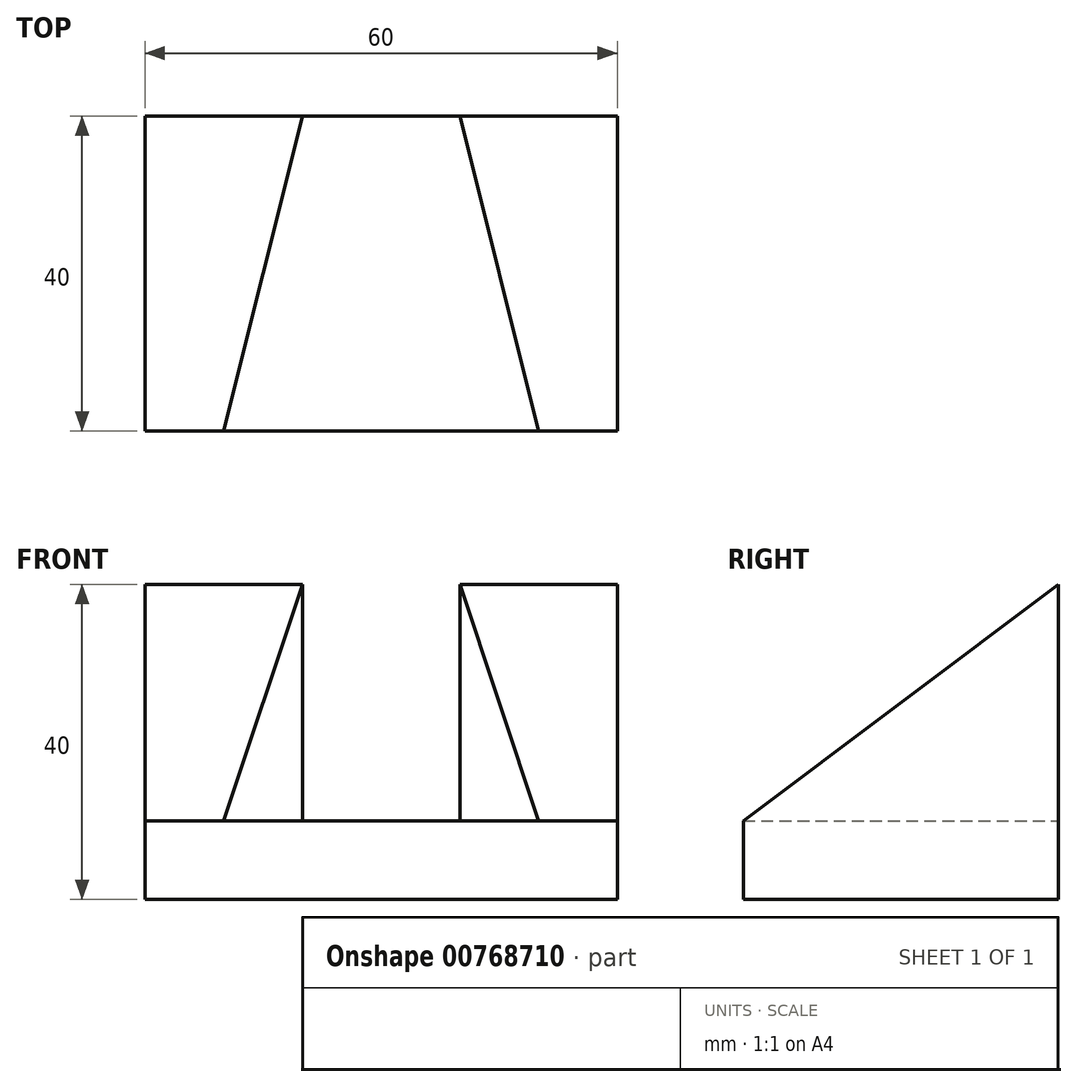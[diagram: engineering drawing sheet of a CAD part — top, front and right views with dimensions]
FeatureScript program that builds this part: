
annotation { "Feature Type Name" : "Feature", "Feature Type Description" : "" }
export const myFeature = defineFeature(function(context is Context, id is Id, definition is map)
    precondition{}
    {
        {
            var Q0;
            Q0=qCreatedBy(makeId("Top.planeOp"),FACE);
            var sketch = newSketch(context, id + "F0", { "sketchPlane" : qUnion([Q0])});
            skLineSegment(sketch, "E0", {"start": v(0, 0) * mm, "end": v(0, 40) * mm});
            skLineSegment(sketch, "E1", {"start": v(0, 40) * mm, "end": v(60, 40) * mm});
            skLineSegment(sketch, "E2", {"start": v(60, 40) * mm, "end": v(60, 0) * mm});
            skLineSegment(sketch, "E3", {"start": v(60, 0) * mm, "end": v(0, 0) * mm});
            skSolve(sketch);
        }
        {
            var Q0;
            Q0=makeQuery(id+"F0.imprint","IMPRINT",FACE,{"disambiguationData":[TD([[makeQuery(id+"F0.imprint","IMPRINT",EDGE,{"derivedFrom":sQuery(id+"F0.wireOp",EDGE,"E0")}),-1.0]])]});
            extrude(context, id + "F1", {"entities" : qUnion([Q0]), "depth" : 40 * mm, "offsetDistance" : 25 * mm});
        }
        {
            var Q0;
            Q0=makeQuery(id+"F1.opExtrude","CAP_FACE",FACE,{"disambiguationData":[OSD([sQuery(id+"F0.wireOp",EDGE,"E0"),sQuery(id+"F0.wireOp",EDGE,"E1"),sQuery(id+"F0.wireOp",EDGE,"E2"),sQuery(id+"F0.wireOp",EDGE,"E3")])],"isStart":false});
            var sketch = newSketch(context, id + "F2", { "sketchPlane" : qUnion([Q0])});
            skLineSegment(sketch, "E4", {"start": v(0, 40) * mm, "end": v(20, 40) * mm});
            skLineSegment(sketch, "E5", {"start": v(40, 40) * mm, "end": v(60, 40) * mm});
            skLineSegment(sketch, "E6", {"start": v(10, 0) * mm, "end": v(0, 0) * mm});
            skLineSegment(sketch, "E7", {"start": v(60, 0) * mm, "end": v(50, 0) * mm});
            skLineSegment(sketch, "E8", {"start": v(10, 0) * mm, "end": v(50, 0) * mm});
            skLineSegment(sketch, "E9", {"start": v(10, 0) * mm, "end": v(20, 40) * mm});
            skLineSegment(sketch, "E10", {"start": v(50, 0) * mm, "end": v(40, 40) * mm});
            skLineSegment(sketch, "E11", {"start": v(40, 40) * mm, "end": v(20, 40) * mm});
            skSolve(sketch);
        }
        {
            var Q0;
            Q0 = qSketchRegion(id + "F2", true);
            extrude(context, id + "F3", {"entities" : qUnion([Q0]), "operationType" : NewBodyOperationType.REMOVE, "oppositeDirection" : true, "depth" : 30 * mm, "offsetDistance" : 25 * mm});
        }
        {
            var Q0;
            Q0=makeQuery(id+"F1.opExtrude","SWEPT_FACE",FACE,{"disambiguationData":[OSD([sQuery(id+"F0.wireOp",EDGE,"E2")])]});
            var sketch = newSketch(context, id + "F4", { "sketchPlane" : qUnion([Q0])});
            skLineSegment(sketch, "E12", {"start": v(0, 0) * mm, "end": v(0, 10) * mm});
            skLineSegment(sketch, "E13", {"start": v(40, 40) * mm, "end": v(0, 10) * mm});
            skLineSegment(sketch, "E14", {"start": v(0, 40) * mm, "end": v(0, 10) * mm});
            skLineSegment(sketch, "E15", {"start": v(0, 40) * mm, "end": v(40, 40) * mm});
            skSolve(sketch);
        }
        {
            var Q0;
            Q0 = qSketchRegion(id + "F4", true);
            extrude(context, id + "F5", {"entities" : qUnion([Q0]), "operationType" : NewBodyOperationType.REMOVE, "oppositeDirection" : true, "depth" : 60 * mm, "offsetDistance" : 25 * mm});
        }
    });
